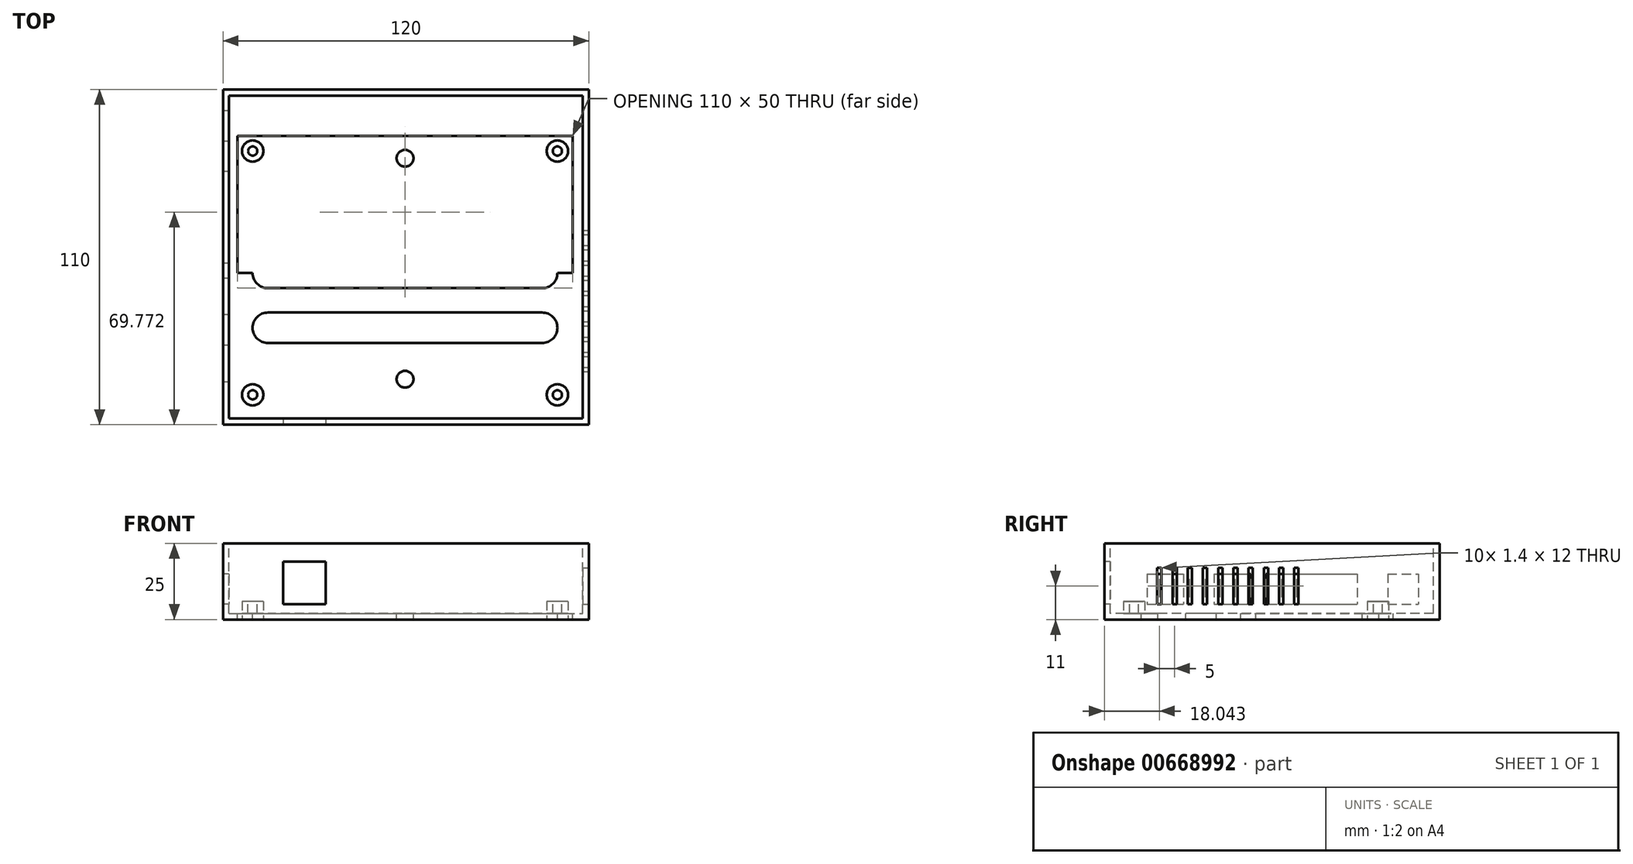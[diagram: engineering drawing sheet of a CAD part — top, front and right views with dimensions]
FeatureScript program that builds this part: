
annotation { "Feature Type Name" : "Feature", "Feature Type Description" : "" }
export const myFeature = defineFeature(function(context is Context, id is Id, definition is map)
    precondition{}
    {
        {
            var Q0;
            Q0=qCreatedBy(makeId("Top.planeOp"),FACE);
            var sketch = newSketch(context, id + "F0", { "sketchPlane" : qUnion([Q0])});
            skLineSegment(sketch, "E0.bottom", {"start": v(60, -55) * mm, "end": v(-60, -55) * mm});
            skLineSegment(sketch, "E0.top", {"start": v(60, 55) * mm, "end": v(-60, 55) * mm});
            skLineSegment(sketch, "E0.left", {"start": v(60, -55) * mm, "end": v(60, 55) * mm});
            skLineSegment(sketch, "E0.right", {"start": v(-60, -55) * mm, "end": v(-60, 55) * mm});
            skPoint(sketch, "E0.middle", {"position": v(0, 0) * mm});
            skSolve(sketch);
        }
        {
            var Q0;
            Q0 = qSketchRegion(id + "F0", true);
            extrude(context, id + "F1", {"entities" : qUnion([Q0]), "depth" : 25 * mm, "offsetDistance" : 25 * mm});
        }
        {
            var Q0;
            Q0=makeQuery(id+"F1.opExtrude","CAP_FACE",FACE,{"disambiguationData":[OSD([sQuery(id+"F0.wireOp",EDGE,"E0.bottom"),sQuery(id+"F0.wireOp",EDGE,"E0.top"),sQuery(id+"F0.wireOp",EDGE,"E0.left"),sQuery(id+"F0.wireOp",EDGE,"E0.right")])],"isStart":false});
            var sketch = newSketch(context, id + "F2", { "sketchPlane" : qUnion([Q0])});
            skLineSegment(sketch, "E1.bottom", {"start": v(-58, 53) * mm, "end": v(58, 53) * mm});
            skLineSegment(sketch, "E1.top", {"start": v(-58, -53) * mm, "end": v(58, -53) * mm});
            skLineSegment(sketch, "E1.left", {"start": v(-58, 53) * mm, "end": v(-58, -53) * mm});
            skLineSegment(sketch, "E1.right", {"start": v(58, 53) * mm, "end": v(58, -53) * mm});
            skSolve(sketch);
        }
        {
            var Q0;
            Q0 = qSketchRegion(id + "F2", true);
            extrude(context, id + "F3", {"entities" : qUnion([Q0]), "operationType" : NewBodyOperationType.REMOVE, "oppositeDirection" : true, "depth" : 23 * mm, "offsetDistance" : 25 * mm});
        }
        {
            var Q0;
            Q0=makeQuery(id+"F3.boolean.opBoolean","COPY",FACE,{"derivedFrom":makeQuery(id+"F3.opExtrude","CAP_FACE",FACE,{"disambiguationData":[OSD([sQuery(id+"F2.wireOp",EDGE,"E1.bottom"),sQuery(id+"F2.wireOp",EDGE,"E1.top"),sQuery(id+"F2.wireOp",EDGE,"E1.left"),sQuery(id+"F2.wireOp",EDGE,"E1.right")])],"isStart":false})});
            var sketch = newSketch(context, id + "F4", { "sketchPlane" : qUnion([Q0])});
            skLineSegment(sketch, "E2.bottom", {"start": v(-55.27, -50.23) * mm, "end": v(54.73, -50.23) * mm});
            skLineSegment(sketch, "E2.top", {"start": v(-55.27, 39.77) * mm, "end": v(54.73, 39.77) * mm});
            skLineSegment(sketch, "E2.left", {"start": v(-55.27, -50.23) * mm, "end": v(-55.27, 39.77) * mm});
            skLineSegment(sketch, "E2.right", {"start": v(54.73, -50.23) * mm, "end": v(54.73, 39.77) * mm});
            skPoint(sketch, "E3.startSnap0", {"position": v(-58, 0) * mm});
            skLineSegment(sketch, "E4", {"start": v(-0.27, 39.77) * mm, "end": v(-0.27, -50.23) * mm});
            skCircle(sketch, "E5", {"center": v(-50.27, 34.77) * mm, "radius": 3.5 * mm});
            skLineSegment(sketch, "E6", {"start": v(-55.27, -5.23) * mm, "end": v(54.73, -5.23) * mm});
            skCircle(sketch, "E7", {"center": v(49.73, 34.77) * mm, "radius": 3.5 * mm});
            skCircle(sketch, "E8", {"center": v(49.73, -45.23) * mm, "radius": 3.5 * mm});
            skCircle(sketch, "E9", {"center": v(-50.27, -45.23) * mm, "radius": 3.5 * mm});
            skLineSegment(sketch, "E10.bottom", {"start": v(44.73, -10.23) * mm, "end": v(-45.27, -10.23) * mm});
            skLineSegment(sketch, "E10.top", {"start": v(44.73, -0.23) * mm, "end": v(-45.27, -0.23) * mm});
            skLineSegment(sketch, "E10.left", {"start": v(49.73, -5.23) * mm, "end": v(49.73, -5.23) * mm});
            skLineSegment(sketch, "E10.right", {"start": v(-50.27, -5.23) * mm, "end": v(-50.27, -5.23) * mm});
            skPoint(sketch, "E10.middle", {"position": v(-0.27, -5.23) * mm});
            skLineSegment(sketch, "E11.bottom", {"start": v(44.73, -28.23) * mm, "end": v(-45.27, -28.23) * mm});
            skLineSegment(sketch, "E11.top", {"start": v(44.73, -18.23) * mm, "end": v(-45.27, -18.23) * mm});
            skLineSegment(sketch, "E11.left", {"start": v(49.73, -23.23) * mm, "end": v(49.73, -23.23) * mm});
            skLineSegment(sketch, "E11.right", {"start": v(-50.27, -23.23) * mm, "end": v(-50.27, -23.23) * mm});
            skPoint(sketch, "E11.middle", {"position": v(-0.27, -23.23) * mm});
            skLineSegment(sketch, "E12.bottom", {"start": v(44.73, 7.77) * mm, "end": v(-45.27, 7.77) * mm});
            skLineSegment(sketch, "E12.top", {"start": v(44.73, 17.77) * mm, "end": v(-45.27, 17.77) * mm});
            skLineSegment(sketch, "E12.left", {"start": v(49.73, 12.77) * mm, "end": v(49.73, 12.77) * mm});
            skLineSegment(sketch, "E12.right", {"start": v(-50.27, 12.77) * mm, "end": v(-50.27, 12.77) * mm});
            skPoint(sketch, "E12.middle", {"position": v(-0.27, 12.77) * mm});
            skPoint(sketch, "E13.visualSharp", {"position": v(-50.27, 17.77) * mm});
            skArc(sketch, "E13.filletArc", {"start": v(-45.27, 17.77) * mm, "mid": v(-48.8, 16.3) * mm, "end": v(-50.27, 12.77) * mm});
            skPoint(sketch, "E14.visualSharp", {"position": v(-50.27, 7.77) * mm});
            skArc(sketch, "E14.filletArc", {"start": v(-50.27, 12.77) * mm, "mid": v(-48.8, 9.24) * mm, "end": v(-45.27, 7.77) * mm});
            skPoint(sketch, "E15.visualSharp", {"position": v(49.73, 17.77) * mm});
            skArc(sketch, "E15.filletArc", {"start": v(49.73, 12.77) * mm, "mid": v(48.26, 16.3) * mm, "end": v(44.73, 17.77) * mm});
            skPoint(sketch, "E16.visualSharp", {"position": v(49.73, 7.77) * mm});
            skArc(sketch, "E16.filletArc", {"start": v(44.73, 7.77) * mm, "mid": v(48.26, 9.24) * mm, "end": v(49.73, 12.77) * mm});
            skPoint(sketch, "E17.visualSharp", {"position": v(49.73, -0.23) * mm});
            skArc(sketch, "E17.filletArc", {"start": v(49.73, -5.23) * mm, "mid": v(48.26, -1.7) * mm, "end": v(44.73, -0.23) * mm});
            skPoint(sketch, "E18.visualSharp", {"position": v(49.73, -10.23) * mm});
            skArc(sketch, "E18.filletArc", {"start": v(44.73, -10.23) * mm, "mid": v(48.26, -8.76) * mm, "end": v(49.73, -5.23) * mm});
            skPoint(sketch, "E19.visualSharp", {"position": v(49.73, -18.23) * mm});
            skArc(sketch, "E19.filletArc", {"start": v(49.73, -23.23) * mm, "mid": v(48.26, -19.7) * mm, "end": v(44.73, -18.23) * mm});
            skPoint(sketch, "E20.visualSharp", {"position": v(49.73, -28.23) * mm});
            skArc(sketch, "E20.filletArc", {"start": v(44.73, -28.23) * mm, "mid": v(48.26, -26.76) * mm, "end": v(49.73, -23.23) * mm});
            skPoint(sketch, "E21.visualSharp", {"position": v(-50.27, -28.23) * mm});
            skArc(sketch, "E21.filletArc", {"start": v(-50.27, -23.23) * mm, "mid": v(-48.8, -26.76) * mm, "end": v(-45.27, -28.23) * mm});
            skPoint(sketch, "E22.visualSharp", {"position": v(-50.27, -18.23) * mm});
            skArc(sketch, "E22.filletArc", {"start": v(-45.27, -18.23) * mm, "mid": v(-48.8, -19.7) * mm, "end": v(-50.27, -23.23) * mm});
            skPoint(sketch, "E23.visualSharp", {"position": v(-50.27, -0.23) * mm});
            skArc(sketch, "E23.filletArc", {"start": v(-45.27, -0.23) * mm, "mid": v(-48.8, -1.7) * mm, "end": v(-50.27, -5.23) * mm});
            skPoint(sketch, "E24.visualSharp", {"position": v(-50.27, -10.23) * mm});
            skArc(sketch, "E24.filletArc", {"start": v(-50.27, -5.23) * mm, "mid": v(-48.8, -8.76) * mm, "end": v(-45.27, -10.23) * mm});
            skCircle(sketch, "E25", {"center": v(-0.27, 32.4) * mm, "radius": 2.75 * mm});
            skCircle(sketch, "E26", {"center": v(-0.27, -40.12) * mm, "radius": 2.75 * mm});
            skSolve(sketch);
        }
        {
            var Q0;
            Q0=makeQuery(id+"F4.imprint","IMPRINT",FACE,{"disambiguationData":[TD([[makeQuery(id+"F4.imprint","IMPRINT",EDGE,{"derivedFrom":sQuery(id+"F4.wireOp",EDGE,"E5")}),1.0]])]});
            var Q1;
            Q1=makeQuery(id+"F4.imprint","IMPRINT",FACE,{"disambiguationData":[TD([[makeQuery(id+"F4.imprint","IMPRINT",EDGE,{"derivedFrom":sQuery(id+"F4.wireOp",EDGE,"E7")}),1.0]])]});
            var Q2;
            Q2=makeQuery(id+"F4.imprint","IMPRINT",FACE,{"disambiguationData":[TD([[makeQuery(id+"F4.imprint","IMPRINT",EDGE,{"derivedFrom":sQuery(id+"F4.wireOp",EDGE,"E8")}),1.0]])]});
            var Q3;
            Q3=makeQuery(id+"F4.imprint","IMPRINT",FACE,{"disambiguationData":[TD([[makeQuery(id+"F4.imprint","IMPRINT",EDGE,{"derivedFrom":sQuery(id+"F4.wireOp",EDGE,"E9")}),1.0]])]});
            var Q4;
            Q4=sQuery(id+"F4.wireOp",EDGE,"E5");
            var Q5;
            Q5=sQuery(id+"F4.wireOp",EDGE,"E7");
            var Q6;
            Q6=sQuery(id+"F4.wireOp",EDGE,"E8");
            var Q7;
            Q7=sQuery(id+"F4.wireOp",EDGE,"E9");
            extrude(context, id + "F5", {"entities" : qUnion([Q0, Q1, Q2, Q3]), "operationType" : NewBodyOperationType.ADD, "surfaceEntities" : qUnion([Q4, Q5, Q6, Q7]), "depth" : 4 * mm, "offsetDistance" : 25 * mm});
        }
        {
            var Q0;
            Q0=makeQuery(id+"F5.opExtrude","CAP_FACE",FACE,{"disambiguationData":[OSD([sQuery(id+"F4.wireOp",EDGE,"E5")])],"isStart":false});
            var sketch = newSketch(context, id + "F6", { "sketchPlane" : qUnion([Q0])});
            skCircle(sketch, "E27", {"center": v(-50.27, 34.77) * mm, "radius": 1.5 * mm});
            skSolve(sketch);
        }
        {
            var Q0;
            Q0 = qSketchRegion(id + "F6", true);
            extrude(context, id + "F7", {"entities" : qUnion([Q0]), "operationType" : NewBodyOperationType.REMOVE, "oppositeDirection" : true, "depth" : 4 * mm, "offsetDistance" : 25 * mm});
        }
        {
            var Q0;
            Q0=makeQuery(id+"F5.opExtrude","CAP_FACE",FACE,{"disambiguationData":[OSD([sQuery(id+"F4.wireOp",EDGE,"E7")])],"isStart":false});
            var sketch = newSketch(context, id + "F8", { "sketchPlane" : qUnion([Q0])});
            skCircle(sketch, "E28", {"center": v(49.73, 34.77) * mm, "radius": 1.5 * mm});
            skSolve(sketch);
        }
        {
            var Q0;
            Q0 = qSketchRegion(id + "F8", true);
            extrude(context, id + "F9", {"entities" : qUnion([Q0]), "operationType" : NewBodyOperationType.REMOVE, "oppositeDirection" : true, "depth" : 4 * mm, "offsetDistance" : 25 * mm});
        }
        {
            var Q0;
            Q0=makeQuery(id+"F5.opExtrude","CAP_FACE",FACE,{"disambiguationData":[OSD([sQuery(id+"F4.wireOp",EDGE,"E8")])],"isStart":false});
            var sketch = newSketch(context, id + "F10", { "sketchPlane" : qUnion([Q0])});
            skCircle(sketch, "E29", {"center": v(49.73, -45.23) * mm, "radius": 1.5 * mm});
            skSolve(sketch);
        }
        {
            var Q0;
            Q0 = qSketchRegion(id + "F10", true);
            extrude(context, id + "F11", {"entities" : qUnion([Q0]), "operationType" : NewBodyOperationType.REMOVE, "oppositeDirection" : true, "depth" : 4 * mm, "offsetDistance" : 25 * mm});
        }
        {
            var Q0;
            Q0=makeQuery(id+"F5.opExtrude","CAP_FACE",FACE,{"disambiguationData":[OSD([sQuery(id+"F4.wireOp",EDGE,"E9")])],"isStart":false});
            var sketch = newSketch(context, id + "F12", { "sketchPlane" : qUnion([Q0])});
            skCircle(sketch, "E30", {"center": v(-50.27, -45.23) * mm, "radius": 1.5 * mm});
            skSolve(sketch);
        }
        {
            var Q0;
            Q0 = qSketchRegion(id + "F12", true);
            extrude(context, id + "F13", {"entities" : qUnion([Q0]), "operationType" : NewBodyOperationType.REMOVE, "oppositeDirection" : true, "depth" : 4 * mm, "offsetDistance" : 25 * mm});
        }
        {
            var Q0;
            Q0=makeQuery(id+"F1.opExtrude","SWEPT_FACE",FACE,{"disambiguationData":[OSD([sQuery(id+"F0.wireOp",EDGE,"E0.bottom")])]});
            var sketch = newSketch(context, id + "F14", { "sketchPlane" : qUnion([Q0])});
            skLineSegment(sketch, "E31.bottom", {"start": v(-40.3, 19) * mm, "end": v(-26.3, 19) * mm});
            skLineSegment(sketch, "E31.top", {"start": v(-40.3, 5) * mm, "end": v(-26.3, 5) * mm});
            skLineSegment(sketch, "E31.left", {"start": v(-40.3, 19) * mm, "end": v(-40.3, 5) * mm});
            skLineSegment(sketch, "E31.right", {"start": v(-26.3, 19) * mm, "end": v(-26.3, 5) * mm});
            skSolve(sketch);
        }
        {
            var Q0;
            Q0 = qSketchRegion(id + "F14", true);
            extrude(context, id + "F15", {"entities" : qUnion([Q0]), "operationType" : NewBodyOperationType.REMOVE, "oppositeDirection" : true, "depth" : 5 * mm, "offsetDistance" : 25 * mm});
        }
        {
            var Q0;
            Q0=makeQuery(id+"F1.opExtrude","SWEPT_FACE",FACE,{"disambiguationData":[OSD([sQuery(id+"F0.wireOp",EDGE,"E0.right")])]});
            var sketch = newSketch(context, id + "F16", { "sketchPlane" : qUnion([Q0])});
            skLineSegment(sketch, "E32.bottom", {"start": v(41, 15) * mm, "end": v(29, 15) * mm});
            skLineSegment(sketch, "E32.top", {"start": v(41, 5) * mm, "end": v(29, 5) * mm});
            skLineSegment(sketch, "E32.left", {"start": v(41, 15) * mm, "end": v(41, 5) * mm});
            skLineSegment(sketch, "E32.right", {"start": v(29, 15) * mm, "end": v(29, 5) * mm});
            skLineSegment(sketch, "E33.bottom", {"start": v(19, 15) * mm, "end": v(7, 15) * mm});
            skLineSegment(sketch, "E33.top", {"start": v(19, 5) * mm, "end": v(7, 5) * mm});
            skLineSegment(sketch, "E33.left", {"start": v(19, 15) * mm, "end": v(19, 5) * mm});
            skLineSegment(sketch, "E33.right", {"start": v(7, 15) * mm, "end": v(7, 5) * mm});
            skLineSegment(sketch, "E34.bottom", {"start": v(2, 15) * mm, "end": v(-28, 15) * mm});
            skLineSegment(sketch, "E34.top", {"start": v(2, 5) * mm, "end": v(-28, 5) * mm});
            skLineSegment(sketch, "E34.left", {"start": v(2, 15) * mm, "end": v(2, 5) * mm});
            skLineSegment(sketch, "E34.right", {"start": v(-28, 15) * mm, "end": v(-28, 5) * mm});
            skLineSegment(sketch, "E35.bottom", {"start": v(-38, 15) * mm, "end": v(-48, 15) * mm});
            skLineSegment(sketch, "E35.top", {"start": v(-38, 5) * mm, "end": v(-48, 5) * mm});
            skLineSegment(sketch, "E35.left", {"start": v(-38, 15) * mm, "end": v(-38, 5) * mm});
            skLineSegment(sketch, "E35.right", {"start": v(-48, 15) * mm, "end": v(-48, 5) * mm});
            skSolve(sketch);
        }
        {
            var Q0;
            Q0 = qSketchRegion(id + "F16", true);
            extrude(context, id + "F17", {"entities" : qUnion([Q0]), "operationType" : NewBodyOperationType.REMOVE, "oppositeDirection" : true, "depth" : 2 * mm, "offsetDistance" : 25 * mm});
        }
        {
            var Q0;
            {var subQ0=sQuery(id+"F4.wireOp",EDGE,"E13.filletArc");Q0=makeQuery(id+"F4.imprint","IMPRINT",FACE,{"disambiguationData":[TD([[makeQuery(id+"F4.imprint","IMPRINT",EDGE,{"derivedFrom":subQ0}),1.0]])]});}
            var Q1;
            {var subQ0=sQuery(id+"F4.wireOp",EDGE,"E15.filletArc");Q1=makeQuery(id+"F4.imprint","IMPRINT",FACE,{"disambiguationData":[TD([[makeQuery(id+"F4.imprint","IMPRINT",EDGE,{"derivedFrom":subQ0}),1.0]])]});}
            extrude(context, id + "F18", {"entities" : qUnion([Q0, Q1]), "operationType" : NewBodyOperationType.REMOVE, "oppositeDirection" : true, "depth" : 25 * mm, "offsetDistance" : 25 * mm});
        }
        {
            var Q0;
            {var subQ0=sQuery(id+"F4.wireOp",EDGE,"E19.filletArc");Q0=makeQuery(id+"F4.imprint","IMPRINT",FACE,{"disambiguationData":[TD([[makeQuery(id+"F4.imprint","IMPRINT",EDGE,{"derivedFrom":subQ0}),1.0]])]});}
            var Q1;
            {var subQ5=sQuery(id+"F4.wireOp",EDGE,"E18.filletArc");Q1=makeQuery(id+"F4.imprint","IMPRINT",FACE,{"disambiguationData":[TD([[makeQuery(id+"F4.imprint","IMPRINT",EDGE,{"derivedFrom":subQ5}),1.0]])]});}
            var Q2;
            {var subQ5=sQuery(id+"F4.wireOp",EDGE,"E23.filletArc");Q2=makeQuery(id+"F4.imprint","IMPRINT",FACE,{"disambiguationData":[TD([[makeQuery(id+"F4.imprint","IMPRINT",EDGE,{"derivedFrom":subQ5}),1.0]])]});}
            var Q3;
            {var subQ5=sQuery(id+"F4.wireOp",EDGE,"E24.filletArc");Q3=makeQuery(id+"F4.imprint","IMPRINT",FACE,{"disambiguationData":[TD([[makeQuery(id+"F4.imprint","IMPRINT",EDGE,{"derivedFrom":subQ5}),1.0]])]});}
            var Q4;
            {var subQ4=sQuery(id+"F4.wireOp",EDGE,"E21.filletArc");Q4=makeQuery(id+"F4.imprint","IMPRINT",FACE,{"disambiguationData":[TD([[makeQuery(id+"F4.imprint","IMPRINT",EDGE,{"derivedFrom":subQ4}),1.0]])]});}
            var Q5;
            {var subQ5=sQuery(id+"F4.wireOp",EDGE,"E17.filletArc");Q5=makeQuery(id+"F4.imprint","IMPRINT",FACE,{"disambiguationData":[TD([[makeQuery(id+"F4.imprint","IMPRINT",EDGE,{"derivedFrom":subQ5}),1.0]])]});}
            extrude(context, id + "F19", {"entities" : qUnion([Q0, Q1, Q2, Q3, Q4, Q5]), "operationType" : NewBodyOperationType.REMOVE, "oppositeDirection" : true, "depth" : 25 * mm, "offsetDistance" : 25 * mm});
        }
        {
            var Q0;
            {var subQ0=sQuery(id+"F4.wireOp",EDGE,"E25");var subQ1=sQuery(id+"F4.wireOp",EDGE,"E4");var subQ2=makeQuery(id+"F4.imprint","INTERSECT",VERTEX,{"disambiguationData":[OD(0.0)],"derivedFrom":[subQ1,subQ0]});Q0=makeQuery(id+"F4.imprint","IMPRINT",FACE,{"disambiguationData":[TD([[makeQuery(id+"F4.imprint","IMPRINT",EDGE,{"disambiguationData":[TD([[subQ2,-1.0]])],"derivedFrom":subQ1}),1.0]])]});}
            var Q1;
            {var subQ0=sQuery(id+"F4.wireOp",EDGE,"E25");var subQ1=sQuery(id+"F4.wireOp",EDGE,"E4");var subQ2=makeQuery(id+"F4.imprint","INTERSECT",VERTEX,{"disambiguationData":[OD(0.0)],"derivedFrom":[subQ1,subQ0]});Q1=makeQuery(id+"F4.imprint","IMPRINT",FACE,{"disambiguationData":[TD([[makeQuery(id+"F4.imprint","IMPRINT",EDGE,{"disambiguationData":[TD([[subQ2,-1.0]])],"derivedFrom":subQ1}),-1.0]])]});}
            var Q2;
            Q2=sQuery(id+"F4.wireOp",EDGE,"E25");
            extrude(context, id + "F20", {"entities" : qUnion([Q0, Q1]), "operationType" : NewBodyOperationType.REMOVE, "surfaceEntities" : qUnion([Q2]), "oppositeDirection" : true, "depth" : 25 * mm, "offsetDistance" : 25 * mm});
        }
        {
            var Q0;
            {var subQ0=sQuery(id+"F4.wireOp",EDGE,"E26");var subQ1=sQuery(id+"F4.wireOp",EDGE,"E4");var subQ2=makeQuery(id+"F4.imprint","INTERSECT",VERTEX,{"disambiguationData":[OD(0.0)],"derivedFrom":[subQ1,subQ0]});Q0=makeQuery(id+"F4.imprint","IMPRINT",FACE,{"disambiguationData":[TD([[makeQuery(id+"F4.imprint","IMPRINT",EDGE,{"disambiguationData":[TD([[subQ2,-1.0]])],"derivedFrom":subQ1}),1.0]])]});}
            var Q1;
            {var subQ0=sQuery(id+"F4.wireOp",EDGE,"E26");var subQ1=sQuery(id+"F4.wireOp",EDGE,"E4");var subQ2=makeQuery(id+"F4.imprint","INTERSECT",VERTEX,{"disambiguationData":[OD(0.0)],"derivedFrom":[subQ1,subQ0]});Q1=makeQuery(id+"F4.imprint","IMPRINT",FACE,{"disambiguationData":[TD([[makeQuery(id+"F4.imprint","IMPRINT",EDGE,{"disambiguationData":[TD([[subQ2,-1.0]])],"derivedFrom":subQ1}),-1.0]])]});}
            var Q2;
            Q2=sQuery(id+"F4.wireOp",EDGE,"E26");
            extrude(context, id + "F21", {"entities" : qUnion([Q0, Q1]), "operationType" : NewBodyOperationType.REMOVE, "surfaceEntities" : qUnion([Q2]), "oppositeDirection" : true, "depth" : 25 * mm, "offsetDistance" : 25 * mm});
        }
        {
            var Q0;
            Q0=makeQuery(id+"F1.opExtrude","SWEPT_FACE",FACE,{"disambiguationData":[OSD([sQuery(id+"F0.wireOp",EDGE,"E0.left")])]});
            var sketch = newSketch(context, id + "F22", { "sketchPlane" : qUnion([Q0])});
            skLineSegment(sketch, "E36.bottom", {"start": v(-36.26, 5) * mm, "end": v(-37.65, 5) * mm});
            skLineSegment(sketch, "E36.top", {"start": v(-36.26, 17) * mm, "end": v(-37.65, 17) * mm});
            skLineSegment(sketch, "E36.left", {"start": v(-36.26, 5) * mm, "end": v(-36.26, 17) * mm});
            skLineSegment(sketch, "E36.right", {"start": v(-37.65, 5) * mm, "end": v(-37.65, 17) * mm});
            skPoint(sketch, "E36.middle", {"position": v(-36.96, 11) * mm});
            skLineSegment(sketch, "E37.1.0.0", {"start": v(-32.65, 5) * mm, "end": v(-32.65, 17) * mm});
            skPoint(sketch, "E37.1.0.1", {"position": v(-31.96, 11) * mm});
            skLineSegment(sketch, "E37.1.0.2", {"start": v(-31.26, 5) * mm, "end": v(-32.65, 5) * mm});
            skLineSegment(sketch, "E37.1.0.3", {"start": v(-31.26, 17) * mm, "end": v(-32.65, 17) * mm});
            skLineSegment(sketch, "E37.1.0.4", {"start": v(-31.26, 5) * mm, "end": v(-31.26, 17) * mm});
            skLineSegment(sketch, "E37.2.0.0", {"start": v(-27.65, 5) * mm, "end": v(-27.65, 17) * mm});
            skPoint(sketch, "E37.2.0.1", {"position": v(-26.96, 11) * mm});
            skLineSegment(sketch, "E37.2.0.2", {"start": v(-26.26, 5) * mm, "end": v(-27.65, 5) * mm});
            skLineSegment(sketch, "E37.2.0.3", {"start": v(-26.26, 17) * mm, "end": v(-27.65, 17) * mm});
            skLineSegment(sketch, "E37.2.0.4", {"start": v(-26.26, 5) * mm, "end": v(-26.26, 17) * mm});
            skLineSegment(sketch, "E37.3.0.0", {"start": v(-22.65, 5) * mm, "end": v(-22.65, 17) * mm});
            skPoint(sketch, "E37.3.0.1", {"position": v(-21.96, 11) * mm});
            skLineSegment(sketch, "E37.3.0.2", {"start": v(-21.26, 5) * mm, "end": v(-22.65, 5) * mm});
            skLineSegment(sketch, "E37.3.0.3", {"start": v(-21.26, 17) * mm, "end": v(-22.65, 17) * mm});
            skLineSegment(sketch, "E37.3.0.4", {"start": v(-21.26, 5) * mm, "end": v(-21.26, 17) * mm});
            skLineSegment(sketch, "E37.4.0.0", {"start": v(-17.65, 5) * mm, "end": v(-17.65, 17) * mm});
            skPoint(sketch, "E37.4.0.1", {"position": v(-16.96, 11) * mm});
            skLineSegment(sketch, "E37.4.0.2", {"start": v(-16.26, 5) * mm, "end": v(-17.65, 5) * mm});
            skLineSegment(sketch, "E37.4.0.3", {"start": v(-16.26, 17) * mm, "end": v(-17.65, 17) * mm});
            skLineSegment(sketch, "E37.4.0.4", {"start": v(-16.26, 5) * mm, "end": v(-16.26, 17) * mm});
            skLineSegment(sketch, "E37.5.0.0", {"start": v(-12.65, 5) * mm, "end": v(-12.65, 17) * mm});
            skPoint(sketch, "E37.5.0.1", {"position": v(-11.96, 11) * mm});
            skLineSegment(sketch, "E37.5.0.2", {"start": v(-11.26, 5) * mm, "end": v(-12.65, 5) * mm});
            skLineSegment(sketch, "E37.5.0.3", {"start": v(-11.26, 17) * mm, "end": v(-12.65, 17) * mm});
            skLineSegment(sketch, "E37.5.0.4", {"start": v(-11.26, 5) * mm, "end": v(-11.26, 17) * mm});
            skLineSegment(sketch, "E37.6.0.0", {"start": v(-7.65, 5) * mm, "end": v(-7.65, 17) * mm});
            skPoint(sketch, "E37.6.0.1", {"position": v(-6.96, 11) * mm});
            skLineSegment(sketch, "E37.6.0.2", {"start": v(-6.26, 5) * mm, "end": v(-7.65, 5) * mm});
            skLineSegment(sketch, "E37.6.0.3", {"start": v(-6.26, 17) * mm, "end": v(-7.65, 17) * mm});
            skLineSegment(sketch, "E37.6.0.4", {"start": v(-6.26, 5) * mm, "end": v(-6.26, 17) * mm});
            skLineSegment(sketch, "E37.7.0.0", {"start": v(-2.65, 5) * mm, "end": v(-2.65, 17) * mm});
            skPoint(sketch, "E37.7.0.1", {"position": v(-1.96, 11) * mm});
            skLineSegment(sketch, "E37.7.0.2", {"start": v(-1.26, 5) * mm, "end": v(-2.65, 5) * mm});
            skLineSegment(sketch, "E37.7.0.3", {"start": v(-1.26, 17) * mm, "end": v(-2.65, 17) * mm});
            skLineSegment(sketch, "E37.7.0.4", {"start": v(-1.26, 5) * mm, "end": v(-1.26, 17) * mm});
            skLineSegment(sketch, "E37.8.0.0", {"start": v(2.35, 5) * mm, "end": v(2.35, 17) * mm});
            skPoint(sketch, "E37.8.0.1", {"position": v(3.04, 11) * mm});
            skLineSegment(sketch, "E37.8.0.2", {"start": v(3.74, 5) * mm, "end": v(2.35, 5) * mm});
            skLineSegment(sketch, "E37.8.0.3", {"start": v(3.74, 17) * mm, "end": v(2.35, 17) * mm});
            skLineSegment(sketch, "E37.8.0.4", {"start": v(3.74, 5) * mm, "end": v(3.74, 17) * mm});
            skLineSegment(sketch, "E37.9.0.0", {"start": v(7.35, 5) * mm, "end": v(7.35, 17) * mm});
            skPoint(sketch, "E37.9.0.1", {"position": v(8.04, 11) * mm});
            skLineSegment(sketch, "E37.9.0.2", {"start": v(8.74, 5) * mm, "end": v(7.35, 5) * mm});
            skLineSegment(sketch, "E37.9.0.3", {"start": v(8.74, 17) * mm, "end": v(7.35, 17) * mm});
            skLineSegment(sketch, "E37.9.0.4", {"start": v(8.74, 5) * mm, "end": v(8.74, 17) * mm});
            skLineSegment(sketch, "E37.direction1", {"start": v(-37.65, 5) * mm, "end": v(-32.65, 5) * mm, "construction": true});
            skSolve(sketch);
        }
        {
            var Q0;
            Q0=makeQuery(id+"F22.imprint","IMPRINT",FACE,{"disambiguationData":[TD([[makeQuery(id+"F22.imprint","IMPRINT",EDGE,{"derivedFrom":sQuery(id+"F22.wireOp",EDGE,"E37.9.0.0")}),-1.0]])]});
            var Q1;
            Q1=makeQuery(id+"F22.imprint","IMPRINT",FACE,{"disambiguationData":[TD([[makeQuery(id+"F22.imprint","IMPRINT",EDGE,{"derivedFrom":sQuery(id+"F22.wireOp",EDGE,"E37.8.0.0")}),-1.0]])]});
            var Q2;
            Q2=makeQuery(id+"F22.imprint","IMPRINT",FACE,{"disambiguationData":[TD([[makeQuery(id+"F22.imprint","IMPRINT",EDGE,{"derivedFrom":sQuery(id+"F22.wireOp",EDGE,"E37.7.0.0")}),-1.0]])]});
            var Q3;
            Q3=makeQuery(id+"F22.imprint","IMPRINT",FACE,{"disambiguationData":[TD([[makeQuery(id+"F22.imprint","IMPRINT",EDGE,{"derivedFrom":sQuery(id+"F22.wireOp",EDGE,"E37.6.0.0")}),-1.0]])]});
            var Q4;
            Q4=makeQuery(id+"F22.imprint","IMPRINT",FACE,{"disambiguationData":[TD([[makeQuery(id+"F22.imprint","IMPRINT",EDGE,{"derivedFrom":sQuery(id+"F22.wireOp",EDGE,"E37.5.0.0")}),-1.0]])]});
            var Q5;
            Q5=makeQuery(id+"F22.imprint","IMPRINT",FACE,{"disambiguationData":[TD([[makeQuery(id+"F22.imprint","IMPRINT",EDGE,{"derivedFrom":sQuery(id+"F22.wireOp",EDGE,"E37.4.0.0")}),-1.0]])]});
            var Q6;
            Q6=makeQuery(id+"F22.imprint","IMPRINT",FACE,{"disambiguationData":[TD([[makeQuery(id+"F22.imprint","IMPRINT",EDGE,{"derivedFrom":sQuery(id+"F22.wireOp",EDGE,"E37.3.0.0")}),-1.0]])]});
            var Q7;
            Q7=makeQuery(id+"F22.imprint","IMPRINT",FACE,{"disambiguationData":[TD([[makeQuery(id+"F22.imprint","IMPRINT",EDGE,{"derivedFrom":sQuery(id+"F22.wireOp",EDGE,"E37.2.0.0")}),-1.0]])]});
            var Q8;
            Q8=makeQuery(id+"F22.imprint","IMPRINT",FACE,{"disambiguationData":[TD([[makeQuery(id+"F22.imprint","IMPRINT",EDGE,{"derivedFrom":sQuery(id+"F22.wireOp",EDGE,"E37.1.0.0")}),-1.0]])]});
            var Q9;
            Q9=makeQuery(id+"F22.imprint","IMPRINT",FACE,{"disambiguationData":[TD([[makeQuery(id+"F22.imprint","IMPRINT",EDGE,{"derivedFrom":sQuery(id+"F22.wireOp",EDGE,"E36.bottom")}),-1.0]])]});
            extrude(context, id + "F23", {"entities" : qUnion([Q0, Q1, Q2, Q3, Q4, Q5, Q6, Q7, Q8, Q9]), "operationType" : NewBodyOperationType.REMOVE, "oppositeDirection" : true, "depth" : 25 * mm, "offsetDistance" : 25 * mm});
        }
    });
